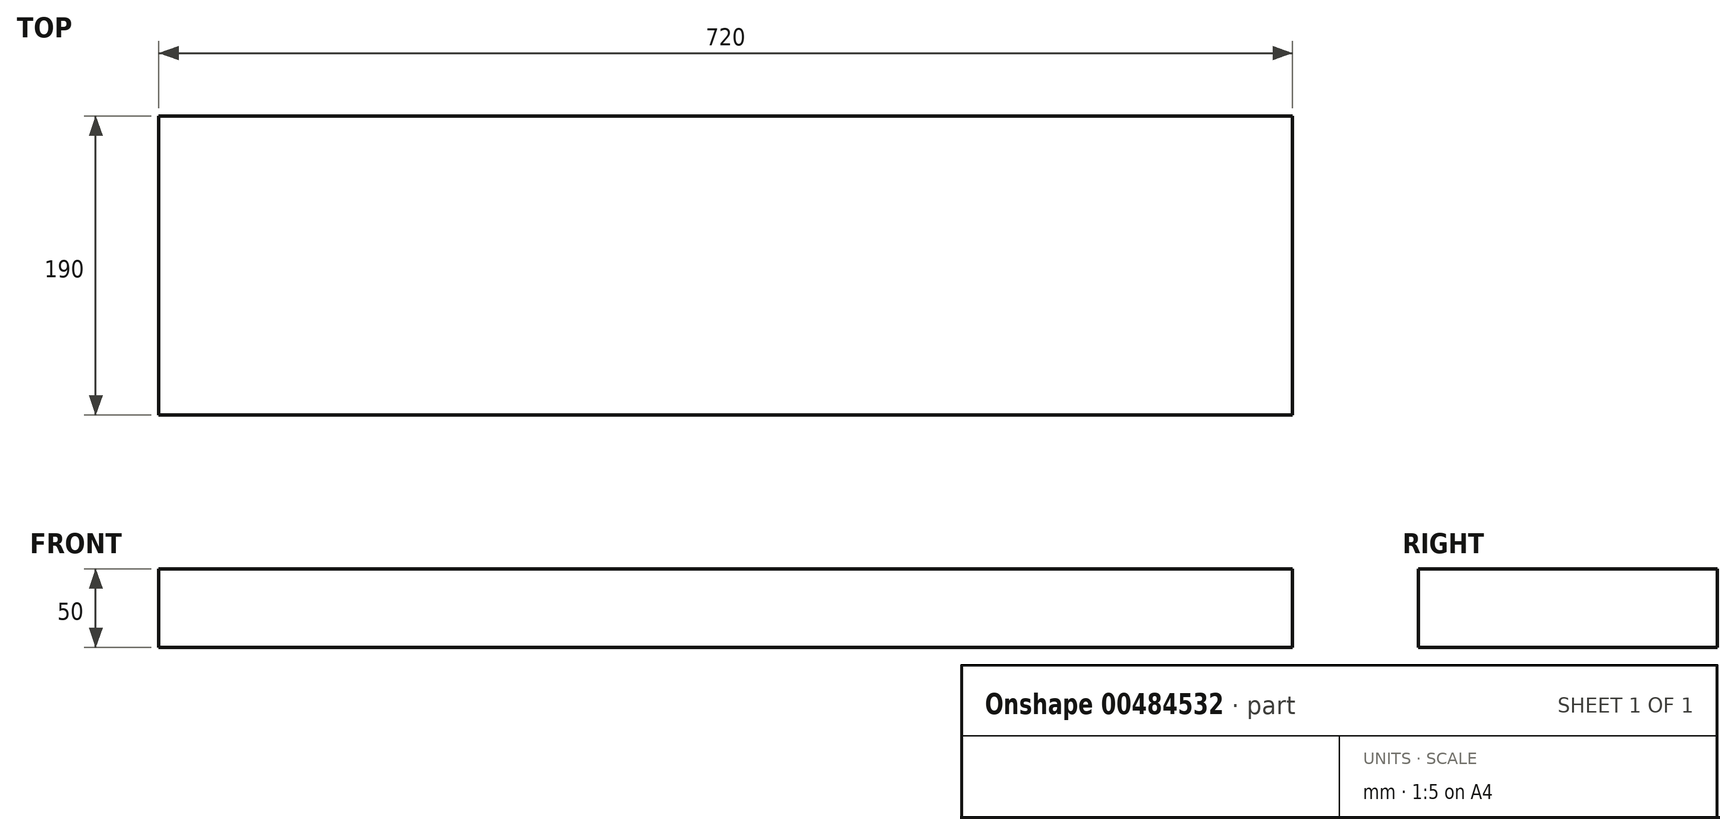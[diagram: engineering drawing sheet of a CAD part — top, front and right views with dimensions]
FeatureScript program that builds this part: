
annotation { "Feature Type Name" : "Feature", "Feature Type Description" : "" }
export const myFeature = defineFeature(function(context is Context, id is Id, definition is map)
    precondition{}
    {
        {
            var Q0;
            Q0=qCreatedBy(makeId("Top.planeOp"),FACE);
            var sketch = newSketch(context, id + "F0", { "sketchPlane" : qUnion([Q0])});
            skLineSegment(sketch, "E0.bottom", {"start": v(-509.87, -280.53) * mm, "end": v(210.13, -280.53) * mm});
            skLineSegment(sketch, "E0.top", {"start": v(-509.87, -90.53) * mm, "end": v(210.13, -90.53) * mm});
            skLineSegment(sketch, "E0.left", {"start": v(-509.87, -280.53) * mm, "end": v(-509.87, -90.53) * mm});
            skLineSegment(sketch, "E0.right", {"start": v(210.13, -280.53) * mm, "end": v(210.13, -90.53) * mm});
            skSolve(sketch);
        }
        {
            var Q0;
            Q0=qSketchRegion(id+"F0",true);
            extrude(context, id + "F1", {"entities" : qUnion([Q0]), "depth" : 50 * mm});
        }
    });
